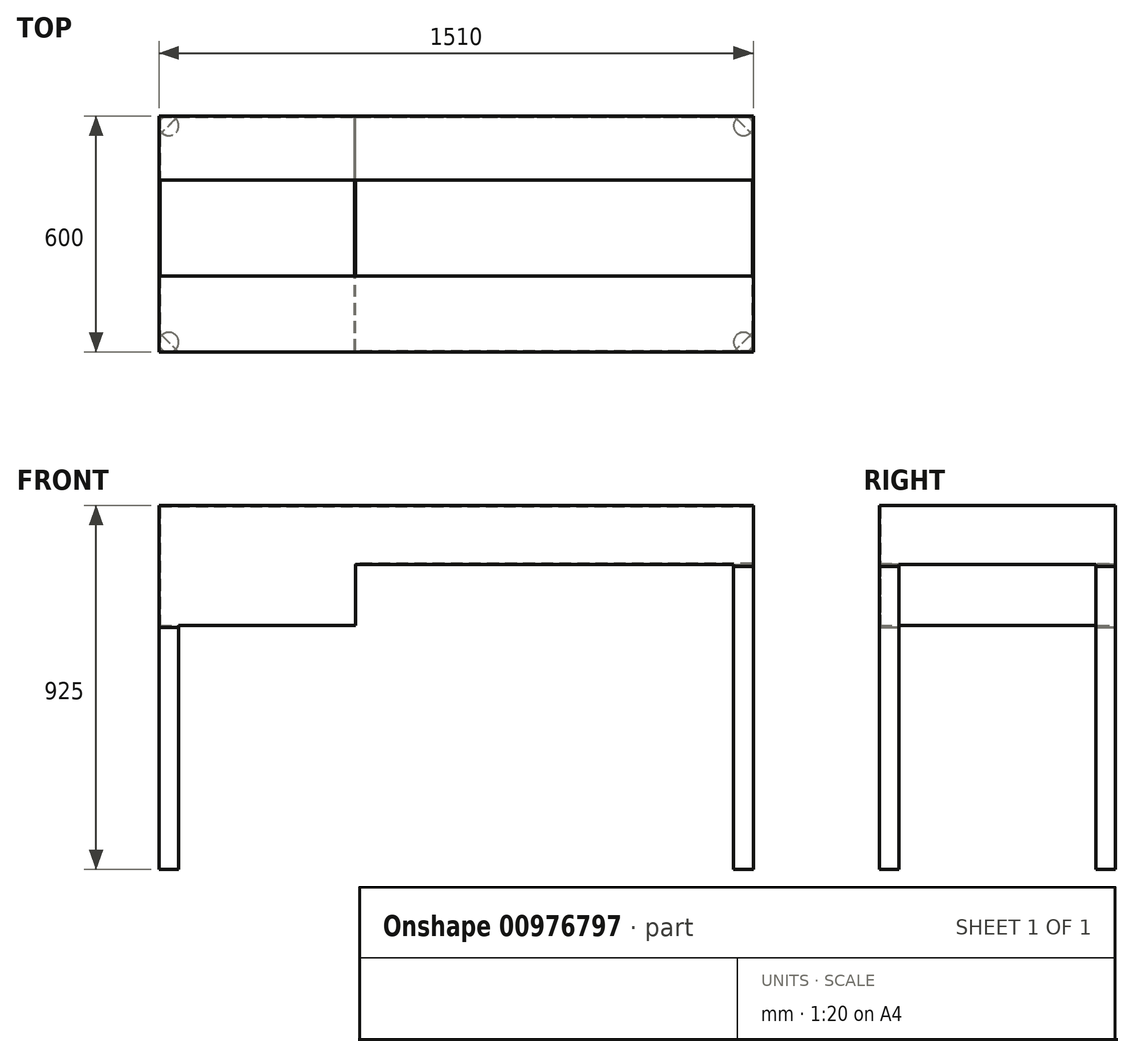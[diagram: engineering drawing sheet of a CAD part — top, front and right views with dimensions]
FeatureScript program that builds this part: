
annotation { "Feature Type Name" : "Feature", "Feature Type Description" : "" }
export const myFeature = defineFeature(function(context is Context, id is Id, definition is map)
    precondition{}
    {
        {
            var Q0;
            Q0=qCreatedBy(makeId("Top.planeOp"),FACE);
            var sketch = newSketch(context, id + "F0", { "sketchPlane" : qUnion([Q0])});
            skLineSegment(sketch, "E0.bottom", {"start": v(-755, 300) * mm, "end": v(755, 300) * mm});
            skLineSegment(sketch, "E0.top", {"start": v(-755, -300) * mm, "end": v(755, -300) * mm});
            skLineSegment(sketch, "E0.left", {"start": v(-755, 300) * mm, "end": v(-755, -300) * mm});
            skLineSegment(sketch, "E0.right", {"start": v(755, 300) * mm, "end": v(755, -300) * mm});
            skLineSegment(sketch, "E1", {"start": v(-881.92, 0) * mm, "end": v(1009.9, 0) * mm, "construction": true});
            skLineSegment(sketch, "E2", {"start": v(0, 644.88) * mm, "end": v(0, -589.68) * mm, "construction": true});
            skSolve(sketch);
        }
        {
            var Q0;
            Q0 = qSketchRegion(id + "F0", true);
            extrude(context, id + "F1", {"entities" : qUnion([Q0]), "depth" : 150 * mm, "offsetDistance" : 25.4 * mm});
        }
        {
            var Q0;
            Q0=makeQuery(id+"F1.opExtrude","CAP_FACE",FACE,{"disambiguationData":[OSD([sQuery(id+"F0.wireOp",EDGE,"E0.bottom"),sQuery(id+"F0.wireOp",EDGE,"E0.top"),sQuery(id+"F0.wireOp",EDGE,"E0.left"),sQuery(id+"F0.wireOp",EDGE,"E0.right")])],"isStart":true});
            shell(context, id + "F2", {"entities" : qUnion([Q0]), "thickness" : 2.54 * mm});
        }
        {
            var Q0;
            Q0=makeQuery(id+"F1.opExtrude","CAP_FACE",FACE,{"disambiguationData":[OSD([sQuery(id+"F0.wireOp",EDGE,"E0.bottom"),sQuery(id+"F0.wireOp",EDGE,"E0.top"),sQuery(id+"F0.wireOp",EDGE,"E0.left"),sQuery(id+"F0.wireOp",EDGE,"E0.right")])],"isStart":true});
            var sketch = newSketch(context, id + "F3", { "sketchPlane" : qUnion([Q0])});
            skLineSegment(sketch, "E3.bottom", {"start": v(-755, 300) * mm, "end": v(-255, 300) * mm});
            skLineSegment(sketch, "E3.top", {"start": v(-755, -300) * mm, "end": v(-255, -300) * mm});
            skLineSegment(sketch, "E3.left", {"start": v(-755, 300) * mm, "end": v(-755, -300) * mm});
            skLineSegment(sketch, "E3.right", {"start": v(-255, 300) * mm, "end": v(-255, -300) * mm});
            skSolve(sketch);
        }
        {
            var Q0;
            Q0 = qSketchRegion(id + "F3", true);
            extrude(context, id + "F4", {"entities" : qUnion([Q0]), "operationType" : NewBodyOperationType.ADD, "depth" : 155 * mm, "offsetDistance" : 25.4 * mm});
        }
        {
            var Q0;
            Q0=makeQuery(id+"F4.opExtrude","CAP_FACE",FACE,{"disambiguationData":[OSD([sQuery(id+"F3.wireOp",EDGE,"E3.bottom"),sQuery(id+"F3.wireOp",EDGE,"E3.top"),sQuery(id+"F3.wireOp",EDGE,"E3.left"),sQuery(id+"F3.wireOp",EDGE,"E3.right")])],"isStart":false});
            var sketch = newSketch(context, id + "F5", { "sketchPlane" : qUnion([Q0])});
            skLineSegment(sketch, "E4.bottom", {"start": v(-752.46, 297.46) * mm, "end": v(-257.54, 297.46) * mm});
            skLineSegment(sketch, "E4.top", {"start": v(-752.46, -297.46) * mm, "end": v(-257.54, -297.46) * mm});
            skLineSegment(sketch, "E4.left", {"start": v(-752.46, 297.46) * mm, "end": v(-752.46, -297.46) * mm});
            skLineSegment(sketch, "E4.right", {"start": v(-257.54, 297.46) * mm, "end": v(-257.54, -297.46) * mm});
            skSolve(sketch);
        }
        {
            var Q0;
            Q0 = qSketchRegion(id + "F5", true);
            var Q1;
            Q1=makeQuery(id+"F2.opShell","OFFSET_FACE",FACE,{"disambiguationData":[OSD([sQuery(id+"F0.wireOp",EDGE,"E0.bottom"),sQuery(id+"F0.wireOp",EDGE,"E0.top"),sQuery(id+"F0.wireOp",EDGE,"E0.left"),sQuery(id+"F0.wireOp",EDGE,"E0.right")])]});
            extrude(context, id + "F6", {"entities" : qUnion([Q0]), "operationType" : NewBodyOperationType.REMOVE, "endBound" : BoundingType.UP_TO_SURFACE, "oppositeDirection" : true, "depth" : 142.24 * mm, "endBoundEntityFace" : qUnion([Q1]), "offsetDistance" : 25.4 * mm});
        }
        {
            var Q0;
            Q0=makeQuery(id+"F1.opExtrude","CAP_FACE",FACE,{"disambiguationData":[OSD([sQuery(id+"F0.wireOp",EDGE,"E0.bottom"),sQuery(id+"F0.wireOp",EDGE,"E0.top"),sQuery(id+"F0.wireOp",EDGE,"E0.left"),sQuery(id+"F0.wireOp",EDGE,"E0.right")])],"isStart":false});
            var sketch = newSketch(context, id + "F7", { "sketchPlane" : qUnion([Q0])});
            skLineSegment(sketch, "E5.bottom", {"start": v(-752.46, 137.54) * mm, "end": v(752.46, 137.54) * mm});
            skLineSegment(sketch, "E5.top", {"start": v(-752.46, -107.46) * mm, "end": v(752.46, -107.46) * mm});
            skLineSegment(sketch, "E5.right", {"start": v(752.46, 137.54) * mm, "end": v(752.46, -107.46) * mm});
            skLineSegment(sketch, "E6", {"start": v(-861.06, 15.04) * mm, "end": v(894.8, 15.04) * mm, "construction": true});
            skPoint(sketch, "E6.startSnap0", {"position": v(-755, 15.04) * mm});
            skLineSegment(sketch, "E7", {"start": v(-752.46, 137.54) * mm, "end": v(-752.46, -107.46) * mm});
            skSolve(sketch);
        }
        {
            var Q0;
            Q0 = qSketchRegion(id + "F7", true);
            extrude(context, id + "F8", {"entities" : qUnion([Q0]), "operationType" : NewBodyOperationType.REMOVE, "oppositeDirection" : true, "depth" : 25.4 * mm, "offsetDistance" : 25.4 * mm});
        }
        {
            var Q0;
            Q0=makeQuery(id+"F1.opExtrude","CAP_FACE",FACE,{"disambiguationData":[OSD([sQuery(id+"F0.wireOp",EDGE,"E0.bottom"),sQuery(id+"F0.wireOp",EDGE,"E0.top"),sQuery(id+"F0.wireOp",EDGE,"E0.left"),sQuery(id+"F0.wireOp",EDGE,"E0.right")])],"isStart":true});
            var sketch = newSketch(context, id + "F9", { "sketchPlane" : qUnion([Q0])});
            skLineSegment(sketch, "E8", {"start": v(755, -300) * mm, "end": v(705, -300) * mm});
            skLineSegment(sketch, "E9", {"start": v(705, -300) * mm, "end": v(755, -250) * mm});
            skLineSegment(sketch, "E10", {"start": v(755, -250) * mm, "end": v(755, -300) * mm});
            skLineSegment(sketch, "E11", {"start": v(755, 300) * mm, "end": v(755, 250) * mm});
            skLineSegment(sketch, "E12", {"start": v(755, 250) * mm, "end": v(705, 300) * mm});
            skLineSegment(sketch, "E13", {"start": v(705, 300) * mm, "end": v(755, 300) * mm});
            skSolve(sketch);
        }
        {
            var Q0;
            Q0 = qSketchRegion(id + "F9", true);
            extrude(context, id + "F10", {"entities" : qUnion([Q0]), "operationType" : NewBodyOperationType.ADD, "depth" : 5 * mm, "offsetDistance" : 25.4 * mm});
        }
        {
            var Q0;
            Q0=makeQuery(id+"F10.opExtrude","CAP_FACE",FACE,{"disambiguationData":[OSD([sQuery(id+"F9.wireOp",EDGE,"E11"),sQuery(id+"F9.wireOp",EDGE,"E12"),sQuery(id+"F9.wireOp",EDGE,"E13")])],"isStart":false});
            var sketch = newSketch(context, id + "F11", { "sketchPlane" : qUnion([Q0])});
            skCircle(sketch, "E14", {"center": v(730, 275) * mm, "radius": 25 * mm});
            skCircle(sketch, "E15", {"center": v(730, -275) * mm, "radius": 25 * mm});
            skSolve(sketch);
        }
        {
            var Q0;
            Q0 = qSketchRegion(id + "F11", true);
            extrude(context, id + "F12", {"entities" : qUnion([Q0]), "operationType" : NewBodyOperationType.ADD, "depth" : 770 * mm, "offsetDistance" : 25.4 * mm});
        }
        {
            var Q0;
            Q0=makeQuery(id+"F4.opExtrude","CAP_FACE",FACE,{"disambiguationData":[OSD([sQuery(id+"F3.wireOp",EDGE,"E3.bottom"),sQuery(id+"F3.wireOp",EDGE,"E3.top"),sQuery(id+"F3.wireOp",EDGE,"E3.left"),sQuery(id+"F3.wireOp",EDGE,"E3.right")])],"isStart":false});
            var sketch = newSketch(context, id + "F13", { "sketchPlane" : qUnion([Q0])});
            skLineSegment(sketch, "E16", {"start": v(-755, -300) * mm, "end": v(-705, -300) * mm});
            skLineSegment(sketch, "E17", {"start": v(-705, -300) * mm, "end": v(-755, -250) * mm});
            skLineSegment(sketch, "E18", {"start": v(-755, -250) * mm, "end": v(-755, -300) * mm});
            skLineSegment(sketch, "E19", {"start": v(-755, 300) * mm, "end": v(-755, 250) * mm});
            skLineSegment(sketch, "E20", {"start": v(-755, 250) * mm, "end": v(-705, 300) * mm});
            skLineSegment(sketch, "E21", {"start": v(-705, 300) * mm, "end": v(-755, 300) * mm});
            skSolve(sketch);
        }
        {
            var Q0;
            Q0 = qSketchRegion(id + "F13", true);
            extrude(context, id + "F14", {"entities" : qUnion([Q0]), "operationType" : NewBodyOperationType.ADD, "depth" : 5 * mm, "offsetDistance" : 25.4 * mm});
        }
        {
            var Q0;
            Q0=makeQuery(id+"F14.opExtrude","CAP_FACE",FACE,{"disambiguationData":[OSD([sQuery(id+"F13.wireOp",EDGE,"E19"),sQuery(id+"F13.wireOp",EDGE,"E20"),sQuery(id+"F13.wireOp",EDGE,"E21")])],"isStart":false});
            var sketch = newSketch(context, id + "F15", { "sketchPlane" : qUnion([Q0])});
            skCircle(sketch, "E22", {"center": v(-730, 275) * mm, "radius": 25 * mm});
            skCircle(sketch, "E23", {"center": v(-730, -275) * mm, "radius": 25 * mm});
            skSolve(sketch);
        }
        {
            var Q0;
            Q0 = qSketchRegion(id + "F15", true);
            var Q1;
            Q1=makeQuery(id+"F12.opExtrude","CAP_FACE",FACE,{"disambiguationData":[OSD([sQuery(id+"F11.wireOp",EDGE,"E14")])],"isStart":false});
            extrude(context, id + "F16", {"entities" : qUnion([Q0]), "operationType" : NewBodyOperationType.ADD, "endBound" : BoundingType.UP_TO_SURFACE, "depth" : 615 * mm, "endBoundEntityFace" : qUnion([Q1]), "offsetDistance" : 25.4 * mm});
        }
        {
            var Q0;
            Q0=makeQuery(id+"F4.opExtrude","SWEPT_FACE",FACE,{"disambiguationData":[OSD([sQuery(id+"F3.wireOp",EDGE,"E3.right")])]});
            var sketch = newSketch(context, id + "F17", { "sketchPlane" : qUnion([Q0])});
            skLineSegment(sketch, "E24.bottom", {"start": v(-297.46, 0) * mm, "end": v(300, 0) * mm});
            skLineSegment(sketch, "E24.top", {"start": v(-297.46, 2.54) * mm, "end": v(300, 2.54) * mm});
            skLineSegment(sketch, "E24.left", {"start": v(-297.46, 0) * mm, "end": v(-297.46, 2.54) * mm});
            skLineSegment(sketch, "E24.right", {"start": v(300, 0) * mm, "end": v(300, 2.54) * mm});
            skSolve(sketch);
        }
        {
            var Q0;
            Q0 = qSketchRegion(id + "F17", true);
            var Q1;
            Q1=makeQuery(id+"F8.boolean.opBoolean","MERGE",FACE,{"derivedFrom":[makeQuery(id+"F2.opShell","OFFSET_FACE",FACE,{"disambiguationData":[OSD([sQuery(id+"F0.wireOp",EDGE,"E0.right")])]})],"fromTools":[makeQuery(id+"F8.opExtrude","SWEPT_FACE",FACE,{"disambiguationData":[OSD([sQuery(id+"F7.wireOp",EDGE,"E5.right")])]})]});
            extrude(context, id + "F18", {"entities" : qUnion([Q0]), "endBound" : BoundingType.UP_TO_SURFACE, "depth" : 25.4 * mm, "endBoundEntityFace" : qUnion([Q1]), "offsetDistance" : 25.4 * mm});
        }
    });
